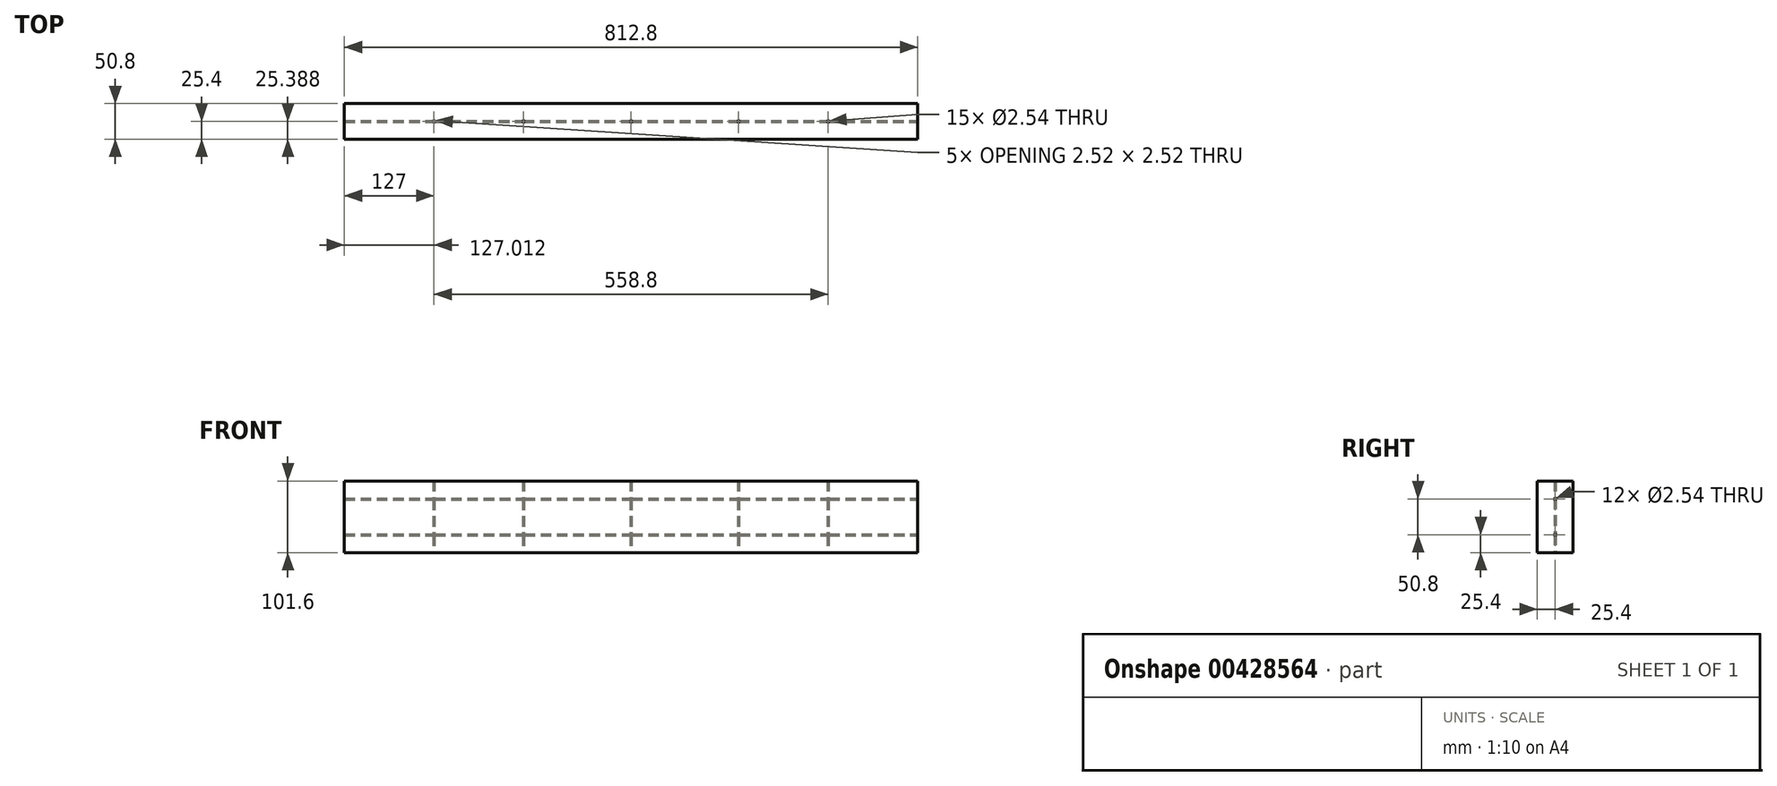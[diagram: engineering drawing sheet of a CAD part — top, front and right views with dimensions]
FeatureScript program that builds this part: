
annotation { "Feature Type Name" : "Feature", "Feature Type Description" : "" }
export const myFeature = defineFeature(function(context is Context, id is Id, definition is map)
    precondition{}
    {
        {
            var Q0;
            Q0=qCreatedBy(makeId("Top.planeOp"),FACE);
            var sketch = newSketch(context, id + "F0", { "sketchPlane" : qUnion([Q0])});
            skLineSegment(sketch, "E0.bottom", {"start": v(-406.4, -25.4) * mm, "end": v(406.4, -25.4) * mm});
            skLineSegment(sketch, "E0.top", {"start": v(-406.4, 25.4) * mm, "end": v(406.4, 25.4) * mm});
            skLineSegment(sketch, "E0.left", {"start": v(-406.4, -25.4) * mm, "end": v(-406.4, 25.4) * mm});
            skLineSegment(sketch, "E0.right", {"start": v(406.4, -25.4) * mm, "end": v(406.4, 25.4) * mm});
            skPoint(sketch, "E0.middle", {"position": v(0, 0) * mm});
            skCircle(sketch, "E1", {"center": v(-279.4, 0) * mm, "radius": 1.27 * mm});
            skCircle(sketch, "E2", {"center": v(-152.4, 0) * mm, "radius": 1.27 * mm});
            skCircle(sketch, "E3", {"center": v(0, 0) * mm, "radius": 1.27 * mm});
            skCircle(sketch, "E4", {"center": v(152.4, 0) * mm, "radius": 1.27 * mm});
            skCircle(sketch, "E5", {"center": v(279.4, 0) * mm, "radius": 1.27 * mm});
            skSolve(sketch);
        }
        {
            var Q0;
            Q0=makeQuery(id+"F0.imprint","IMPRINT",FACE,{"disambiguationData":[TD([[makeQuery(id+"F0.imprint","IMPRINT",EDGE,{"derivedFrom":sQuery(id+"F0.wireOp",EDGE,"E0.bottom")}),1.0]])]});
            extrude(context, id + "F1", {"entities" : qUnion([Q0]), "depth" : 101.6 * mm});
        }
        {
            var Q0;
            Q0=makeQuery(id+"F1.opExtrude","SWEPT_FACE",FACE,{"disambiguationData":[OSD([sQuery(id+"F0.wireOp",EDGE,"E0.right")])]});
            var sketch = newSketch(context, id + "F2", { "sketchPlane" : qUnion([Q0])});
            skCircle(sketch, "E6", {"center": v(0, 76.2) * mm, "radius": 1.27 * mm});
            skCircle(sketch, "E7", {"center": v(0, 25.4) * mm, "radius": 1.27 * mm});
            skSolve(sketch);
        }
        {
            var Q0;
            Q0=makeQuery(id+"F2.imprint","IMPRINT",FACE,{"disambiguationData":[TD([[makeQuery(id+"F2.imprint","IMPRINT",EDGE,{"derivedFrom":sQuery(id+"F2.wireOp",EDGE,"E6")}),1.0]])]});
            var Q1;
            Q1=makeQuery(id+"F2.imprint","IMPRINT",FACE,{"disambiguationData":[TD([[makeQuery(id+"F2.imprint","IMPRINT",EDGE,{"derivedFrom":sQuery(id+"F2.wireOp",EDGE,"E7")}),1.0]])]});
            extrude(context, id + "F3", {"entities" : qUnion([Q0, Q1]), "operationType" : NewBodyOperationType.REMOVE, "endBound" : BoundingType.THROUGH_ALL, "oppositeDirection" : true, "depth" : 25.4 * mm});
        }
    });
